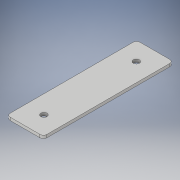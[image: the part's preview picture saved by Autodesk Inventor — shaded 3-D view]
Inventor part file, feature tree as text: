
AUTODESK INVENTOR PART (.ipt)
format: ipt  version: 2019.4 (Build 234330000, 330)  size: 144,384 bytes
history: native  units: in
note: dims shown in document units (in); Inventor stores cm internally (conversion verified against a paired STEP export)
features: other x2, sheet_metal_op x1, sketch x1
ambient origin geometry x8: Origin, YZ Plane, XZ Plane, XY Plane, X Axis, Y Axis, Z Axis, Center Point
bodies: Solid1 (feature_tree)
feature tree (4):
  sheet_metal_op  "Face1"
  sketch  "Sketch1"  dims[d0=1.5in d1=5.31in d2=0.25in d3=0.77in d4=0.25in d5=3.78in d6=0.14in d7=0.12in]
  other  "Plate1"
  other  "Definition1"
